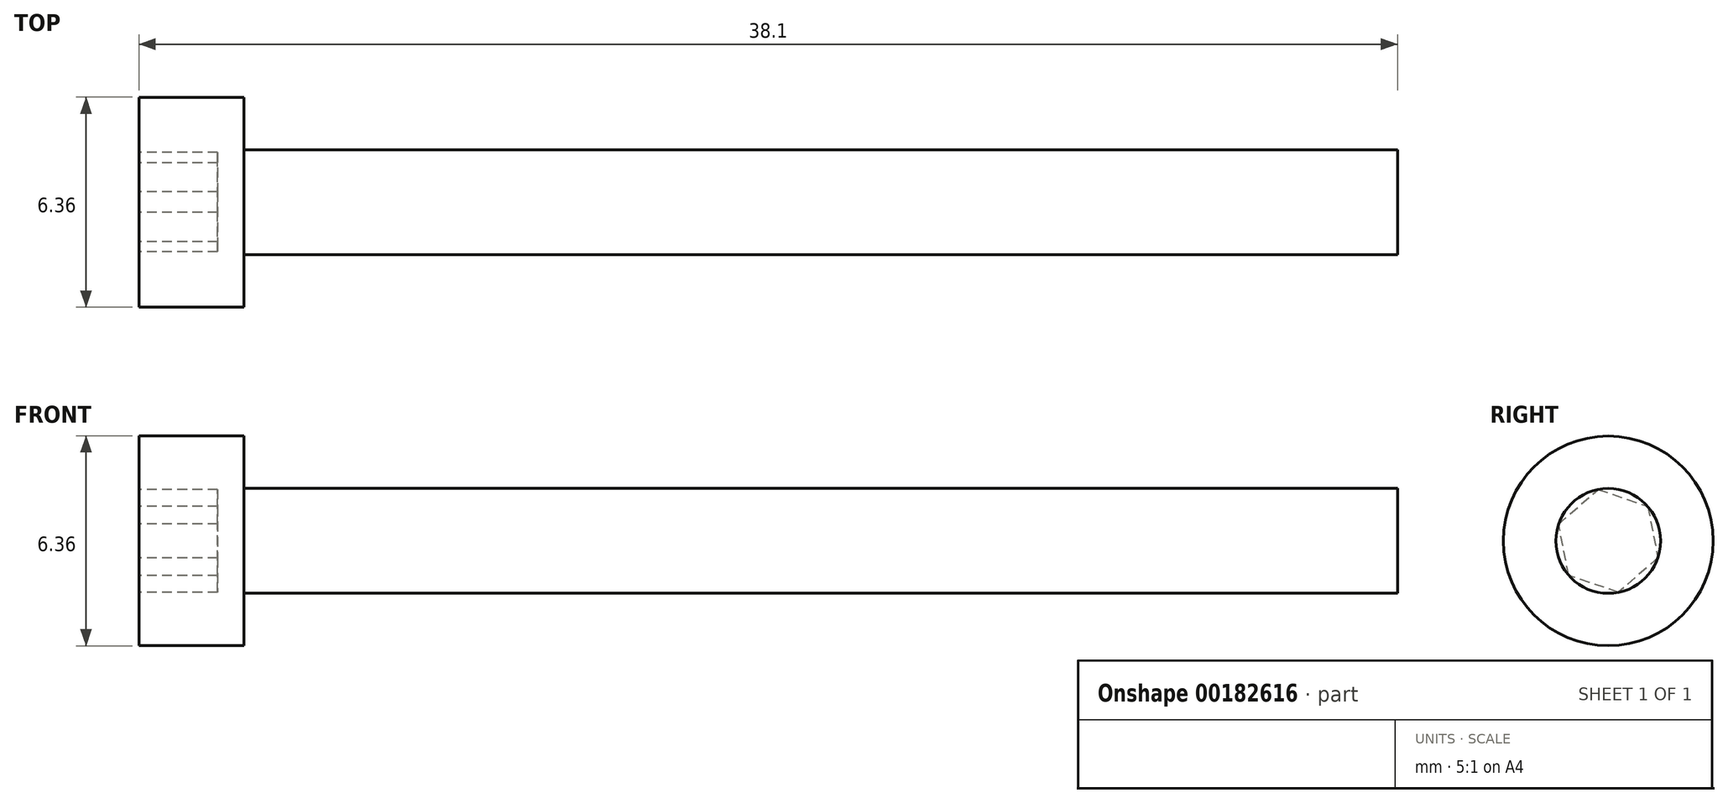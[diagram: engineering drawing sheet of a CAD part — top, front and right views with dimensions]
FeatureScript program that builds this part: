
annotation { "Feature Type Name" : "Feature", "Feature Type Description" : "" }
export const myFeature = defineFeature(function(context is Context, id is Id, definition is map)
    precondition{}
    {
        {
            var Q0;
            Q0=qCreatedBy(makeId("Right.planeOp"),FACE);
            var sketch = newSketch(context, id + "F0", { "sketchPlane" : qUnion([Q0])});
            skCircle(sketch, "E0", {"center": v(0, 0) * mm, "radius": 3.18 * mm});
            skCircle(sketch, "E1.cCircle", {"center": v(0, 0) * mm, "radius": 1.37 * mm, "construction": true});
            skLineSegment(sketch, "E1.0", {"start": v(1.5, -0.51) * mm, "end": v(0.3, -1.56) * mm});
            skLineSegment(sketch, "E1.1", {"start": v(0.3, -1.56) * mm, "end": v(-1.2, -1.05) * mm});
            skLineSegment(sketch, "E1.2", {"start": v(-1.2, -1.05) * mm, "end": v(-1.5, 0.51) * mm});
            skLineSegment(sketch, "E1.3", {"start": v(-1.5, 0.51) * mm, "end": v(-0.3, 1.56) * mm});
            skLineSegment(sketch, "E1.4", {"start": v(-0.3, 1.56) * mm, "end": v(1.2, 1.05) * mm});
            skLineSegment(sketch, "E1.5", {"start": v(1.2, 1.05) * mm, "end": v(1.5, -0.51) * mm});
            skPoint(sketch, "E1.0.midPoint", {"position": v(0.9, -1.03) * mm});
            skSolve(sketch);
        }
        {
            var Q0;
            Q0=makeQuery(id+"F0.imprint","IMPRINT",FACE,{"disambiguationData":[TD([[makeQuery(id+"F0.imprint","IMPRINT",EDGE,{"derivedFrom":sQuery(id+"F0.wireOp",EDGE,"E0")}),1.0]])]});
            var Q1;
            Q1=makeQuery(id+"F0.imprint","IMPRINT",FACE,{"disambiguationData":[TD([[makeQuery(id+"F0.imprint","IMPRINT",EDGE,{"derivedFrom":sQuery(id+"F0.wireOp",EDGE,"E1.0")}),-1.0]])]});
            extrude(context, id + "F1", {"entities" : qUnion([Q0, Q1]), "depth" : 3.17 * mm});
        }
        {
            var Q0;
            Q0=makeQuery(id+"F1.opExtrude","CAP_FACE",FACE,{"disambiguationData":[OSD([sQuery(id+"F0.wireOp",EDGE,"E0")])],"isStart":false});
            var sketch = newSketch(context, id + "F2", { "sketchPlane" : qUnion([Q0])});
            skCircle(sketch, "E2", {"center": v(0, 0) * mm, "radius": 1.59 * mm});
            skSolve(sketch);
        }
        {
            var Q0;
            Q0 = qSketchRegion(id + "F2", true);
            extrude(context, id + "F3", {"entities" : qUnion([Q0]), "operationType" : NewBodyOperationType.ADD, "depth" : 34.92 * mm});
        }
        {
            var Q0;
            Q0=makeQuery(id+"F0.imprint","IMPRINT",FACE,{"disambiguationData":[TD([[makeQuery(id+"F0.imprint","IMPRINT",EDGE,{"derivedFrom":sQuery(id+"F0.wireOp",EDGE,"E1.0")}),-1.0]])]});
            extrude(context, id + "F4", {"entities" : qUnion([Q0]), "operationType" : NewBodyOperationType.REMOVE, "depth" : 2.38 * mm});
        }
    });
